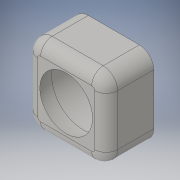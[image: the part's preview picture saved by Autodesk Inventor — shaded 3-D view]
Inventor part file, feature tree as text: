
AUTODESK INVENTOR PART (.ipt)
format: ipt  version: 2016 (Build 200138000, 138)  size: 157,696 bytes
history: native  units: in
note: dims shown in document units (in); Inventor stores cm internally (conversion verified against a paired STEP export)
features: sketch x3, extrude x2, fillet x2, reference x2, plane x1, revolve x1
ambient origin geometry x8: Origin, YZ Plane, XZ Plane, XY Plane, X Axis, Y Axis, Z Axis, Center Point
bodies: Solid1 (feature_tree)
feature tree (11):
  extrude  "Extrusion1"  Depth=0.0787in
  plane  "Work Plane1"
  revolve  "Revolution1"  [1 undecoded]
  extrude  "Extrusion3"  [1 undecoded]
  fillet  "Fillet1"  [1 undecoded]
  fillet  "Fillet2"  Radius=0.268in
  sketch  "Sketch1"  dims[d0=0.0787in d1=0.0787in]
  reference  "Reference1"
  sketch  "Sketch2"  dims[d2=0.0787in d3=0.0787in]
  reference  "Reference2"
  sketch  "Sketch4"  dims[d4=0.4134in d5=0.0in d6=-0.3465in d7=90.0deg d10=0.268in d11=0.0in d12=0.125in d13=0.1in]
note: 3 required parameter values undecoded (feature->parameter linkage not recoverable at this tier; creation-order binding heuristic only, values carry confidence <= 0.55)